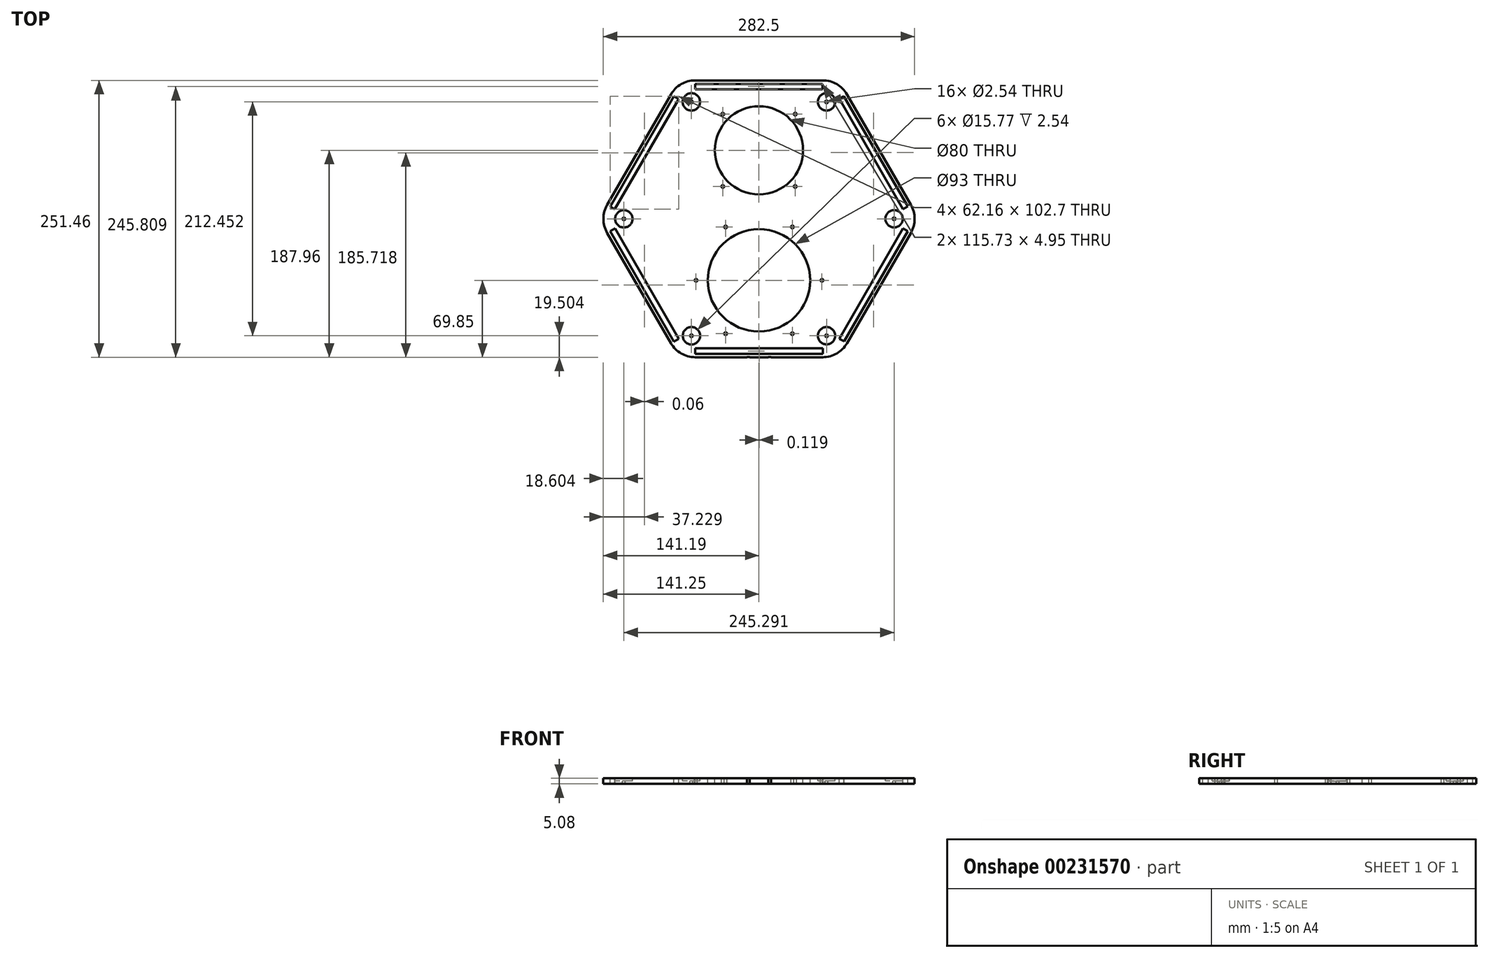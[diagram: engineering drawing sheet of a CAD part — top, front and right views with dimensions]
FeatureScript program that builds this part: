
annotation { "Feature Type Name" : "Feature", "Feature Type Description" : "" }
export const myFeature = defineFeature(function(context is Context, id is Id, definition is map)
    precondition{}
    {
        {
            var Q0;
            Q0=qCreatedBy(makeId("Top.planeOp"),FACE);
            var sketch = newSketch(context, id + "F0", { "sketchPlane" : qUnion([Q0])});
            skCircle(sketch, "E0.cCircle", {"center": v(0, 0) * mm, "radius": 125.73 * mm, "construction": true});
            skLineSegment(sketch, "E0.0", {"start": v(-137.85, 12.7) * mm, "end": v(-79.92, 113.03) * mm});
            skLineSegment(sketch, "E0.1", {"start": v(-57.93, 125.73) * mm, "end": v(57.93, 125.73) * mm});
            skLineSegment(sketch, "E0.2", {"start": v(79.92, 113.03) * mm, "end": v(137.85, 12.7) * mm});
            skLineSegment(sketch, "E0.3", {"start": v(137.85, -12.7) * mm, "end": v(79.92, -113.03) * mm});
            skLineSegment(sketch, "E0.4", {"start": v(57.93, -125.73) * mm, "end": v(-57.93, -125.73) * mm});
            skLineSegment(sketch, "E0.5", {"start": v(-79.92, -113.03) * mm, "end": v(-137.85, -12.7) * mm});
            skPoint(sketch, "E0.0.midPoint", {"position": v(-108.89, 62.87) * mm});
            skPoint(sketch, "E1.visualSharp", {"position": v(-72.6, 125.73) * mm});
            skArc(sketch, "E1.filletArc", {"start": v(-57.93, 125.73) * mm, "mid": v(-70.63, 122.33) * mm, "end": v(-79.92, 113.03) * mm});
            skPoint(sketch, "E2.visualSharp", {"position": v(72.6, 125.73) * mm});
            skArc(sketch, "E2.filletArc", {"start": v(79.92, 113.03) * mm, "mid": v(70.63, 122.33) * mm, "end": v(57.93, 125.73) * mm});
            skPoint(sketch, "E3.visualSharp", {"position": v(145.18, 0) * mm});
            skArc(sketch, "E3.filletArc", {"start": v(137.85, -12.7) * mm, "mid": v(141.25, 0) * mm, "end": v(137.85, 12.7) * mm});
            skPoint(sketch, "E4.visualSharp", {"position": v(72.6, -125.73) * mm});
            skArc(sketch, "E4.filletArc", {"start": v(57.93, -125.73) * mm, "mid": v(70.63, -122.33) * mm, "end": v(79.92, -113.03) * mm});
            skPoint(sketch, "E5.visualSharp", {"position": v(-72.6, -125.73) * mm});
            skArc(sketch, "E5.filletArc", {"start": v(-79.92, -113.03) * mm, "mid": v(-70.63, -122.33) * mm, "end": v(-57.93, -125.73) * mm});
            skPoint(sketch, "E6.visualSharp", {"position": v(-145.18, 0) * mm});
            skArc(sketch, "E6.filletArc", {"start": v(-137.85, 12.7) * mm, "mid": v(-141.25, 0) * mm, "end": v(-137.85, -12.7) * mm});
            skSolve(sketch);
        }
        {
            var Q0;
            Q0 = qSketchRegion(id + "F0", true);
            extrude(context, id + "F1", {"entities" : qUnion([Q0]), "depth" : 5.08 * mm});
        }
        {
            var Q0;
            Q0=makeQuery(id+"F1.opExtrude","CAP_FACE",FACE,{"disambiguationData":[OSD([sQuery(id+"F0.wireOp",EDGE,"E0.0"),sQuery(id+"F0.wireOp",EDGE,"E0.1"),sQuery(id+"F0.wireOp",EDGE,"E0.2"),sQuery(id+"F0.wireOp",EDGE,"E0.3"),sQuery(id+"F0.wireOp",EDGE,"E0.4"),sQuery(id+"F0.wireOp",EDGE,"E0.5"),sQuery(id+"F0.wireOp",EDGE,"E1.filletArc"),sQuery(id+"F0.wireOp",EDGE,"E2.filletArc"),sQuery(id+"F0.wireOp",EDGE,"E3.filletArc"),sQuery(id+"F0.wireOp",EDGE,"E4.filletArc"),sQuery(id+"F0.wireOp",EDGE,"E5.filletArc"),sQuery(id+"F0.wireOp",EDGE,"E6.filletArc")])],"isStart":false});
            var sketch = newSketch(context, id + "F2", { "sketchPlane" : qUnion([Q0])});
            skCircle(sketch, "E7", {"center": v(0, 62.23) * mm, "radius": 40 * mm});
            skCircle(sketch, "E8", {"center": v(0, -55.88) * mm, "radius": 46.5 * mm});
            skLineSegment(sketch, "E9", {"start": v(-77.97, -55.88) * mm, "end": v(84.44, -55.88) * mm, "construction": true});
            skCircle(sketch, "E10", {"center": v(0, -55.88) * mm, "radius": 61.65 * mm, "construction": true});
            skCircle(sketch, "E11", {"center": v(0, 62.23) * mm, "radius": 51.75 * mm, "construction": true});
            skCircle(sketch, "E12", {"center": v(0, -55.88) * mm, "radius": 57.15 * mm, "construction": true});
            skCircle(sketch, "E13", {"center": v(57.15, -55.88) * mm, "radius": 1.27 * mm});
            skLineSegment(sketch, "E14", {"start": v(0, -55.88) * mm, "end": v(0, -25.93) * mm, "construction": true});
            skLineSegment(sketch, "E15", {"start": v(0, -55.88) * mm, "end": v(30.28, -7.41) * mm, "construction": true});
            skLineSegment(sketch, "E16", {"start": v(0, -55.88) * mm, "end": v(30.28, -104.35) * mm, "construction": true});
            skCircle(sketch, "E17", {"center": v(30.28, -7.41) * mm, "radius": 1.27 * mm});
            skCircle(sketch, "E18", {"center": v(30.28, -104.35) * mm, "radius": 1.27 * mm});
            skCircle(sketch, "E19.MirrorC", {"center": v(-30.28, -7.41) * mm, "radius": 1.27 * mm});
            skCircle(sketch, "E20.MirrorC", {"center": v(-30.28, -104.35) * mm, "radius": 1.27 * mm});
            skCircle(sketch, "E21.MirrorC", {"center": v(-57.15, -55.88) * mm, "radius": 1.27 * mm});
            skCircle(sketch, "E22", {"center": v(0, 62.23) * mm, "radius": 46.5 * mm, "construction": true});
            skLineSegment(sketch, "E23", {"start": v(0, 62.23) * mm, "end": v(-32.88, 95.11) * mm, "construction": true});
            skCircle(sketch, "E24", {"center": v(-32.88, 95.11) * mm, "radius": 1.27 * mm});
            skCircle(sketch, "E25", {"center": v(-32.88, 29.35) * mm, "radius": 1.27 * mm});
            skCircle(sketch, "E26", {"center": v(32.88, 29.35) * mm, "radius": 1.27 * mm});
            skCircle(sketch, "E27", {"center": v(32.88, 95.11) * mm, "radius": 1.27 * mm});
            skSolve(sketch);
        }
        {
            var Q0;
            Q0 = qSketchRegion(id + "F2", true);
            extrude(context, id + "F3", {"entities" : qUnion([Q0]), "operationType" : NewBodyOperationType.REMOVE, "oppositeDirection" : true, "depth" : 25.4 * mm});
        }
        {
            var Q0;
            Q0=makeQuery(id+"F1.opExtrude","CAP_FACE",FACE,{"disambiguationData":[OSD([sQuery(id+"F0.wireOp",EDGE,"E0.0"),sQuery(id+"F0.wireOp",EDGE,"E0.1"),sQuery(id+"F0.wireOp",EDGE,"E0.2"),sQuery(id+"F0.wireOp",EDGE,"E0.3"),sQuery(id+"F0.wireOp",EDGE,"E0.4"),sQuery(id+"F0.wireOp",EDGE,"E0.5"),sQuery(id+"F0.wireOp",EDGE,"E1.filletArc"),sQuery(id+"F0.wireOp",EDGE,"E2.filletArc"),sQuery(id+"F0.wireOp",EDGE,"E3.filletArc"),sQuery(id+"F0.wireOp",EDGE,"E4.filletArc"),sQuery(id+"F0.wireOp",EDGE,"E5.filletArc"),sQuery(id+"F0.wireOp",EDGE,"E6.filletArc")])],"isStart":false});
            var sketch = newSketch(context, id + "F4", { "sketchPlane" : qUnion([Q0])});
            skLineSegment(sketch, "E28", {"start": v(-57.93, 122.56) * mm, "end": v(-57.93, 117.6) * mm});
            skLineSegment(sketch, "E29", {"start": v(-57.93, 117.6) * mm, "end": v(57.8, 117.6) * mm});
            skLineSegment(sketch, "E30", {"start": v(57.8, 117.6) * mm, "end": v(57.8, 122.56) * mm});
            skLineSegment(sketch, "E31.1.0", {"start": v(-135.1, 11.11) * mm, "end": v(-130.8, 8.64) * mm});
            skLineSegment(sketch, "E31.1.1", {"start": v(-130.8, 8.64) * mm, "end": v(-72.94, 108.86) * mm});
            skLineSegment(sketch, "E31.1.2", {"start": v(-72.94, 108.86) * mm, "end": v(-77.23, 111.34) * mm});
            skLineSegment(sketch, "E31.2.0", {"start": v(-77.17, -111.44) * mm, "end": v(-72.88, -108.97) * mm});
            skLineSegment(sketch, "E31.2.1", {"start": v(-72.88, -108.97) * mm, "end": v(-130.75, -8.74) * mm});
            skLineSegment(sketch, "E31.2.2", {"start": v(-130.75, -8.74) * mm, "end": v(-135.04, -11.22) * mm});
            skLineSegment(sketch, "E31.3.0", {"start": v(57.93, -122.55) * mm, "end": v(57.93, -117.6) * mm});
            skLineSegment(sketch, "E31.3.1", {"start": v(57.93, -117.6) * mm, "end": v(-57.8, -117.6) * mm});
            skLineSegment(sketch, "E31.3.2", {"start": v(-57.8, -117.6) * mm, "end": v(-57.8, -122.55) * mm});
            skLineSegment(sketch, "E31.4.0", {"start": v(135.1, -11.11) * mm, "end": v(130.8, -8.64) * mm});
            skLineSegment(sketch, "E31.4.1", {"start": v(130.8, -8.64) * mm, "end": v(72.94, -108.86) * mm});
            skLineSegment(sketch, "E31.4.2", {"start": v(72.94, -108.86) * mm, "end": v(77.23, -111.34) * mm});
            skLineSegment(sketch, "E31.5.0", {"start": v(77.17, 111.44) * mm, "end": v(72.88, 108.97) * mm});
            skLineSegment(sketch, "E31.5.1", {"start": v(72.88, 108.97) * mm, "end": v(130.75, 8.74) * mm});
            skLineSegment(sketch, "E31.5.2", {"start": v(130.75, 8.74) * mm, "end": v(135.04, 11.22) * mm});
            skPoint(sketch, "E31.center", {"position": v(0, 0) * mm});
            skLineSegment(sketch, "E32", {"start": v(-57.93, 122.56) * mm, "end": v(57.8, 122.56) * mm});
            skLineSegment(sketch, "E33.1.0", {"start": v(-135.1, 11.11) * mm, "end": v(-77.23, 111.34) * mm});
            skLineSegment(sketch, "E33.2.0", {"start": v(-77.17, -111.44) * mm, "end": v(-135.04, -11.22) * mm});
            skLineSegment(sketch, "E33.3.0", {"start": v(57.93, -122.56) * mm, "end": v(-57.8, -122.56) * mm});
            skLineSegment(sketch, "E33.4.0", {"start": v(135.1, -11.11) * mm, "end": v(77.23, -111.34) * mm});
            skLineSegment(sketch, "E33.5.0", {"start": v(77.17, 111.44) * mm, "end": v(135.04, 11.22) * mm});
            skSolve(sketch);
        }
        {
            var Q0;
            Q0=makeQuery(id+"F4.imprint","IMPRINT",FACE,{"disambiguationData":[TD([[makeQuery(id+"F4.imprint","IMPRINT",EDGE,{"derivedFrom":sQuery(id+"F4.wireOp",EDGE,"E31.2.0")}),1.0]])]});
            var Q1;
            Q1=makeQuery(id+"F4.imprint","IMPRINT",FACE,{"disambiguationData":[TD([[makeQuery(id+"F4.imprint","IMPRINT",EDGE,{"derivedFrom":sQuery(id+"F4.wireOp",EDGE,"E31.1.0")}),1.0]])]});
            var Q2;
            Q2=makeQuery(id+"F4.imprint","IMPRINT",FACE,{"disambiguationData":[TD([[makeQuery(id+"F4.imprint","IMPRINT",EDGE,{"derivedFrom":sQuery(id+"F4.wireOp",EDGE,"E28")}),1.0]])]});
            var Q3;
            Q3=makeQuery(id+"F4.imprint","IMPRINT",FACE,{"disambiguationData":[TD([[makeQuery(id+"F4.imprint","IMPRINT",EDGE,{"derivedFrom":sQuery(id+"F4.wireOp",EDGE,"E31.5.0")}),1.0]])]});
            var Q4;
            Q4=makeQuery(id+"F4.imprint","IMPRINT",FACE,{"disambiguationData":[TD([[makeQuery(id+"F4.imprint","IMPRINT",EDGE,{"derivedFrom":sQuery(id+"F4.wireOp",EDGE,"E31.4.0")}),1.0]])]});
            var Q5;
            Q5=makeQuery(id+"F4.imprint","IMPRINT",FACE,{"disambiguationData":[TD([[makeQuery(id+"F4.imprint","IMPRINT",EDGE,{"derivedFrom":sQuery(id+"F4.wireOp",EDGE,"E31.3.0")}),1.0]])]});
            extrude(context, id + "F5", {"entities" : qUnion([Q0, Q1, Q2, Q3, Q4, Q5]), "operationType" : NewBodyOperationType.REMOVE, "endBound" : BoundingType.THROUGH_ALL, "oppositeDirection" : true, "depth" : 25.4 * mm});
        }
        {
            var Q0;
            Q0=makeQuery(id+"F4.imprint","IMPRINT",FACE,{"disambiguationData":[TD([[makeQuery(id+"F4.imprint","IMPRINT",EDGE,{"derivedFrom":sQuery(id+"F4.wireOp",EDGE,"E28")}),-1.0]])]});
            var sketch = newSketch(context, id + "F6", { "sketchPlane" : qUnion([Q0])});
            skCircle(sketch, "E34", {"center": v(-61.34, 106.2) * mm, "radius": 7.89 * mm});
            skArc(sketch, "E35", {"start": v(-57.93, 117.6) * mm, "mid": v(-66.61, 115.26) * mm, "end": v(-72.94, 108.86) * mm, "construction": true});
            skLineSegment(sketch, "E36", {"start": v(-66.61, 115.26) * mm, "end": v(-61.34, 106.2) * mm, "construction": true});
            skPoint(sketch, "E37", {"position": v(-65.31, 113.02) * mm});
            skCircle(sketch, "E38.1.0", {"center": v(-122.65, -0.02) * mm, "radius": 7.89 * mm});
            skCircle(sketch, "E38.2.0", {"center": v(-61.3, -106.23) * mm, "radius": 7.89 * mm});
            skCircle(sketch, "E38.3.0", {"center": v(61.34, -106.2) * mm, "radius": 7.89 * mm});
            skCircle(sketch, "E38.4.0", {"center": v(122.65, 0.02) * mm, "radius": 7.89 * mm});
            skCircle(sketch, "E38.5.0", {"center": v(61.3, 106.23) * mm, "radius": 7.89 * mm});
            skPoint(sketch, "E38.center", {"position": v(0, 0) * mm});
            skSolve(sketch);
        }
        {
            var Q0;
            Q0=makeQuery(id+"F6.imprint","IMPRINT",FACE,{"disambiguationData":[TD([[makeQuery(id+"F6.imprint","IMPRINT",EDGE,{"derivedFrom":sQuery(id+"F6.wireOp",EDGE,"E34")}),1.0]])]});
            var Q1;
            Q1=makeQuery(id+"F6.imprint","IMPRINT",FACE,{"disambiguationData":[TD([[makeQuery(id+"F6.imprint","IMPRINT",EDGE,{"derivedFrom":sQuery(id+"F6.wireOp",EDGE,"E38.5.0")}),1.0]])]});
            var Q2;
            Q2=makeQuery(id+"F6.imprint","IMPRINT",FACE,{"disambiguationData":[TD([[makeQuery(id+"F6.imprint","IMPRINT",EDGE,{"derivedFrom":sQuery(id+"F6.wireOp",EDGE,"E38.4.0")}),1.0]])]});
            var Q3;
            Q3=makeQuery(id+"F6.imprint","IMPRINT",FACE,{"disambiguationData":[TD([[makeQuery(id+"F6.imprint","IMPRINT",EDGE,{"derivedFrom":sQuery(id+"F6.wireOp",EDGE,"E38.3.0")}),1.0]])]});
            var Q4;
            Q4=makeQuery(id+"F6.imprint","IMPRINT",FACE,{"disambiguationData":[TD([[makeQuery(id+"F6.imprint","IMPRINT",EDGE,{"derivedFrom":sQuery(id+"F6.wireOp",EDGE,"E38.2.0")}),1.0]])]});
            var Q5;
            Q5=makeQuery(id+"F6.imprint","IMPRINT",FACE,{"disambiguationData":[TD([[makeQuery(id+"F6.imprint","IMPRINT",EDGE,{"derivedFrom":sQuery(id+"F6.wireOp",EDGE,"E38.1.0")}),1.0]])]});
            extrude(context, id + "F7", {"entities" : qUnion([Q0, Q1, Q2, Q3, Q4, Q5]), "operationType" : NewBodyOperationType.REMOVE, "oppositeDirection" : true, "depth" : 2.54 * mm});
        }
        {
            var Q0;
            Q0=makeQuery(id+"F7.boolean.opBoolean","COPY",FACE,{"derivedFrom":makeQuery(id+"F7.opExtrude","CAP_FACE",FACE,{"disambiguationData":[OSD([sQuery(id+"F6.wireOp",EDGE,"E34")])],"isStart":false})});
            var sketch = newSketch(context, id + "F8", { "sketchPlane" : qUnion([Q0])});
            skCircle(sketch, "E39", {"center": v(-61.34, 106.2) * mm, "radius": 1.27 * mm});
            skCircle(sketch, "E40", {"center": v(61.3, 106.23) * mm, "radius": 1.27 * mm});
            skCircle(sketch, "E41", {"center": v(-61.3, -106.23) * mm, "radius": 1.27 * mm});
            skCircle(sketch, "E42", {"center": v(61.34, -106.2) * mm, "radius": 1.27 * mm});
            skCircle(sketch, "E43", {"center": v(122.65, 0.02) * mm, "radius": 1.27 * mm});
            skCircle(sketch, "E44", {"center": v(-122.65, -0.02) * mm, "radius": 1.27 * mm});
            skSolve(sketch);
        }
        {
            var Q0;
            Q0 = qSketchRegion(id + "F8", true);
            extrude(context, id + "F9", {"entities" : qUnion([Q0]), "operationType" : NewBodyOperationType.REMOVE, "endBound" : BoundingType.THROUGH_ALL, "oppositeDirection" : true, "depth" : 25.4 * mm});
        }
        {
            var Q0;
            Q0=makeQuery(id+"F1.opExtrude","CAP_FACE",FACE,{"disambiguationData":[OSD([sQuery(id+"F0.wireOp",EDGE,"E0.0"),sQuery(id+"F0.wireOp",EDGE,"E0.1"),sQuery(id+"F0.wireOp",EDGE,"E0.2"),sQuery(id+"F0.wireOp",EDGE,"E0.3"),sQuery(id+"F0.wireOp",EDGE,"E0.4"),sQuery(id+"F0.wireOp",EDGE,"E0.5"),sQuery(id+"F0.wireOp",EDGE,"E1.filletArc"),sQuery(id+"F0.wireOp",EDGE,"E2.filletArc"),sQuery(id+"F0.wireOp",EDGE,"E3.filletArc"),sQuery(id+"F0.wireOp",EDGE,"E4.filletArc"),sQuery(id+"F0.wireOp",EDGE,"E5.filletArc"),sQuery(id+"F0.wireOp",EDGE,"E6.filletArc")])],"isStart":false});
            var sketch = newSketch(context, id + "F10", { "sketchPlane" : qUnion([Q0])});
            skPoint(sketch, "E45", {"position": v(0, -122.56) * mm});
            skPoint(sketch, "E46", {"position": v(9.58, -122.56) * mm});
            skPoint(sketch, "E47", {"position": v(-9.53, -122.56) * mm});
            skLineSegment(sketch, "E48.bottom", {"start": v(-10.8, -125.73) * mm, "end": v(-8.26, -125.73) * mm});
            skLineSegment(sketch, "E48.top", {"start": v(-10.8, -125.48) * mm, "end": v(-8.25, -125.48) * mm});
            skLineSegment(sketch, "E48.left", {"start": v(-10.8, -125.73) * mm, "end": v(-10.8, -125.48) * mm});
            skLineSegment(sketch, "E48.right", {"start": v(-8.25, -125.73) * mm, "end": v(-8.25, -125.48) * mm});
            skLineSegment(sketch, "E49.bottom", {"start": v(8.31, -125.73) * mm, "end": v(10.85, -125.73) * mm});
            skLineSegment(sketch, "E49.top", {"start": v(8.31, -125.48) * mm, "end": v(10.85, -125.48) * mm});
            skLineSegment(sketch, "E49.left", {"start": v(8.31, -125.73) * mm, "end": v(8.31, -125.48) * mm});
            skLineSegment(sketch, "E49.right", {"start": v(10.85, -125.73) * mm, "end": v(10.85, -125.48) * mm});
            skPoint(sketch, "E50", {"position": v(-9.53, -125.48) * mm});
            skPoint(sketch, "E51", {"position": v(9.58, -125.48) * mm});
            skSolve(sketch);
        }
        {
            var Q0;
            Q0 = qSketchRegion(id + "F10", true);
            extrude(context, id + "F11", {"entities" : qUnion([Q0]), "operationType" : NewBodyOperationType.REMOVE, "endBound" : BoundingType.THROUGH_ALL, "oppositeDirection" : true, "depth" : 25.4 * mm});
        }
    });
